# Revit family: LUNA II SWIVEL BATH OUTLET
name_source: partatom
category: Plumbing Fixtures
units: mm (PartAtom-declared; Revit-internal decimal feet)

## family parameters
Cut with Voids When Loaded = Yes
Host = Face
OmniClass Number = 23.45.55.17
OmniClass Title = Mixing Faucets
Part Type = Normal
Room Calculation Point = No
Round Connector Dimension = Use Diameter
Shared = No

## types (4) — shared parameters
Assembly Code = D2020300
CW Connection = Yes
HW Connection = Yes
Manufacturer = GWA Bathrooms & Kitchens
URL = https://www.caroma.com.au
Vent Connection = No
Waste Connection = No
zero-valued in all types: Default Elevation

## per-type parameters (varying)
| type | Base_Material | Model |
| LUNA II SWIVEL BATH OUTLET 220 CH | GWA_Metal-Chrome | 68207C |
| LUNA II SWIVEL BATH OUTLET 220 BL | GWA-Metal-Black | 68207BL |
| LUNA II SWIVEL BATH OUTLET 220 BB | GWA_Metal-Brushed-Brass | 68207BB |
| LUNA II SWIVEL BATH OUTLET 220 BN | GWA_Metal-Brushed-Nickel | 68207BN |

note: column(s) folded — value = type name in every type: Description

## geometry (parser evidence)
native form markers: Sweep x2
no freeform markers — native parametric forms only
